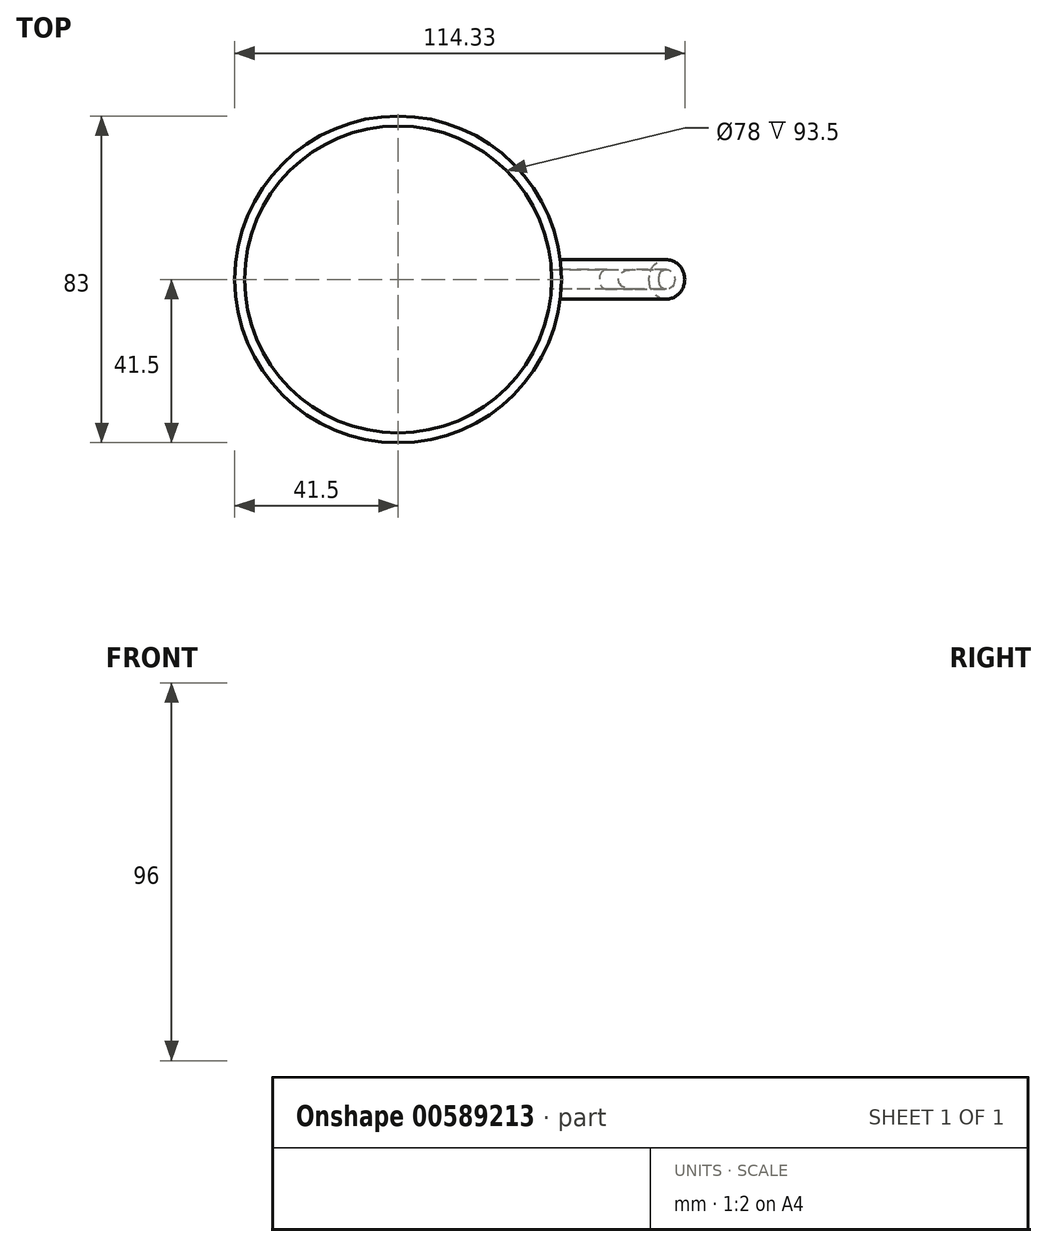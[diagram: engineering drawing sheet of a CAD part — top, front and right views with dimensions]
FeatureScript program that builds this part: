
annotation { "Feature Type Name" : "Feature", "Feature Type Description" : "" }
export const myFeature = defineFeature(function(context is Context, id is Id, definition is map)
    precondition{}
    {
        {
            var Q0;
            Q0=qCreatedBy(makeId("Top.planeOp"),FACE);
            var sketch = newSketch(context, id + "F0", { "sketchPlane" : qUnion([Q0])});
            skCircle(sketch, "E0", {"center": v(0, 0) * mm, "radius": 41.5 * mm});
            skSolve(sketch);
        }
        {
            var Q0;
            Q0=makeQuery(id+"F0.imprint","IMPRINT",FACE,{"disambiguationData":[TD([[makeQuery(id+"F0.imprint","IMPRINT",EDGE,{"derivedFrom":sQuery(id+"F0.wireOp",EDGE,"E0")}),1.0]])]});
            extrude(context, id + "F1", {"entities" : qUnion([Q0]), "depth" : 96 * mm, "offsetDistance" : 25 * mm});
        }
        {
            var Q0;
            Q0=qCreatedBy(makeId("Front.planeOp"),FACE);
            var sketch = newSketch(context, id + "F2", { "sketchPlane" : qUnion([Q0])});
            skFitSpline(sketch, "E1", {"points": [v(30.84, 70.29) * mm, v(51.8, 78.57) * mm, v(67.82, 72.26) * mm, v(66.95, 46.1) * mm, v(60.06, 18.92) * mm, v(38.53, 22.2) * mm], "startDerivative": vector(69.16, 58.9) * mm, "endDerivative": vector(-125.97, 49.04) * mm});
            skSolve(sketch);
        }
        {
            var Q0;
            Q0=qCreatedBy(makeId("Right.planeOp"),FACE);
            cPlane(context, id + "F3", {"entities" : qUnion([Q0]), "cplaneType" : CPlaneType.OFFSET, "offset" : 41.5 * mm, "width" : 150 * mm, "height" : 150 * mm});
        }
        {
            var Q0;
            Q0=qCreatedBy(id+"F3.planeOp",FACE);
            var sketch = newSketch(context, id + "F4", { "sketchPlane" : qUnion([Q0])});
            skCircle(sketch, "E2", {"center": v(0, 22.35) * mm, "radius": 5 * mm});
            skSolve(sketch);
        }
        {
            var Q0;
            Q0 = qSketchRegion(id + "F4", true);
            var Q1;
            Q1=sQuery(id+"F2.wireOp",EDGE,"E1");
            sweep(context, id + "F5", {"operationType" : NewBodyOperationType.ADD, "profiles" : qUnion([Q0]), "path" : qUnion([Q1])});
        }
        {
            var Q0;
            Q0=makeQuery(id+"F1.opExtrude","CAP_FACE",FACE,{"disambiguationData":[OSD([sQuery(id+"F0.wireOp",EDGE,"E0")])],"isStart":false});
            shell(context, id + "F6", {"entities" : qUnion([Q0]), "thickness" : 2.5 * mm});
        }
        {
            var Q0;
            Q0=makeQuery(id+"F1.opExtrude","CAP_EDGE",EDGE,{"disambiguationData":[OSD([sQuery(id+"F0.wireOp",EDGE,"E0")])],"isStart":false});
            fillet(context, id + "F7", {"entities" : qUnion([Q0]), "radius" : 5 * mm, "tangentPropagation" : true, "allowEdgeOverflow" : false});
        }
    });
